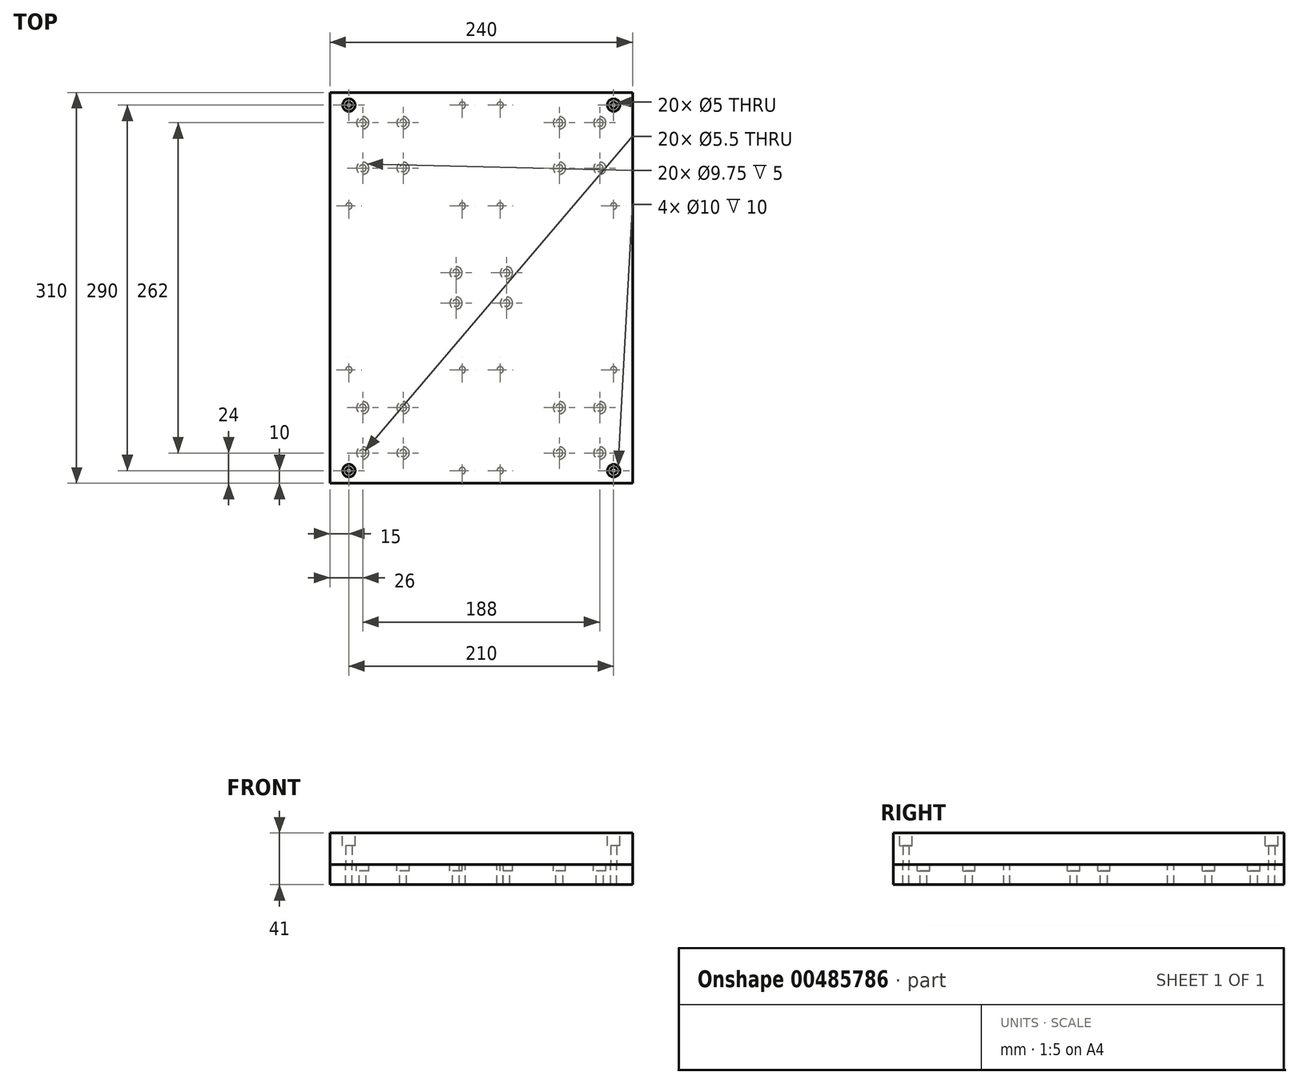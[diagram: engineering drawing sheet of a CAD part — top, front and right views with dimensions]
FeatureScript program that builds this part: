
annotation { "Feature Type Name" : "Feature", "Feature Type Description" : "" }
export const myFeature = defineFeature(function(context is Context, id is Id, definition is map)
    precondition{}
    {
        {
            var Q0;
            Q0=qCreatedBy(makeId("Top.planeOp"),FACE);
            var sketch = newSketch(context, id + "F0", { "sketchPlane" : qUnion([Q0])});
            skLineSegment(sketch, "E0.bottom", {"start": v(120, 155) * mm, "end": v(-120, 155) * mm});
            skLineSegment(sketch, "E0.top", {"start": v(120, -155) * mm, "end": v(-120, -155) * mm});
            skLineSegment(sketch, "E0.left", {"start": v(120, 155) * mm, "end": v(120, -155) * mm});
            skLineSegment(sketch, "E0.right", {"start": v(-120, 155) * mm, "end": v(-120, -155) * mm});
            skPoint(sketch, "E0.middle", {"position": v(0, 0) * mm});
            skLineSegment(sketch, "E1", {"start": v(120, 113) * mm, "end": v(-120, 113) * mm, "construction": true});
            skLineSegment(sketch, "E2", {"start": v(78, 155) * mm, "end": v(78, -155) * mm, "construction": true});
            skLineSegment(sketch, "E3", {"start": v(62, 155) * mm, "end": v(62, -155) * mm, "construction": true});
            skLineSegment(sketch, "E4", {"start": v(94, 155) * mm, "end": v(94, -155) * mm, "construction": true});
            skLineSegment(sketch, "E5", {"start": v(120, 95) * mm, "end": v(-120, 95) * mm, "construction": true});
            skLineSegment(sketch, "E6", {"start": v(120, 131) * mm, "end": v(-120, 131) * mm, "construction": true});
            skPoint(sketch, "E7", {"position": v(94, 131) * mm});
            skPoint(sketch, "E8", {"position": v(94, 95) * mm});
            skPoint(sketch, "E9", {"position": v(62, 95) * mm});
            skPoint(sketch, "E10", {"position": v(62, 131) * mm});
            skLineSegment(sketch, "E11", {"start": v(-62, 155) * mm, "end": v(-62, -155) * mm, "construction": true});
            skLineSegment(sketch, "E12", {"start": v(-78, 155) * mm, "end": v(-78, -155) * mm, "construction": true});
            skLineSegment(sketch, "E13", {"start": v(-94, 155) * mm, "end": v(-94, -155) * mm, "construction": true});
            skLineSegment(sketch, "E14", {"start": v(120, -113) * mm, "end": v(-120, -113) * mm, "construction": true});
            skLineSegment(sketch, "E15", {"start": v(120, -131) * mm, "end": v(-120, -131) * mm, "construction": true});
            skLineSegment(sketch, "E16", {"start": v(120, -95) * mm, "end": v(-120, -95) * mm, "construction": true});
            skPoint(sketch, "E17", {"position": v(-62, 131) * mm});
            skPoint(sketch, "E18", {"position": v(-94, 131) * mm});
            skPoint(sketch, "E19", {"position": v(-62, 95) * mm});
            skPoint(sketch, "E20", {"position": v(-94, 95) * mm});
            skPoint(sketch, "E21", {"position": v(94, -95) * mm});
            skPoint(sketch, "E22", {"position": v(94, -131) * mm});
            skPoint(sketch, "E23", {"position": v(62, -95) * mm});
            skPoint(sketch, "E24", {"position": v(62, -131) * mm});
            skPoint(sketch, "E25", {"position": v(-62, -95) * mm});
            skPoint(sketch, "E26", {"position": v(-62, -131) * mm});
            skPoint(sketch, "E27", {"position": v(-94, -131) * mm});
            skPoint(sketch, "E28", {"position": v(-94, -95) * mm});
            skLineSegment(sketch, "E29.bottom", {"start": v(20, -12) * mm, "end": v(-20, -12) * mm, "construction": true});
            skLineSegment(sketch, "E29.top", {"start": v(20, 12) * mm, "end": v(-20, 12) * mm, "construction": true});
            skLineSegment(sketch, "E29.left", {"start": v(20, -12) * mm, "end": v(20, 12) * mm, "construction": true});
            skLineSegment(sketch, "E29.right", {"start": v(-20, -12) * mm, "end": v(-20, 12) * mm, "construction": true});
            skSolve(sketch);
        }
        {
            var Q0;
            Q0=qSketchRegion(id+"F0",true);
            extrude(context, id + "F1", {"entities" : qUnion([Q0]), "oppositeDirection" : true, "depth" : 16 * mm});
        }
        {
            var Q0;
            Q0=sQuery(id+"F0.wireOp",VERTEX,"E7");
            var Q1;
            Q1=sQuery(id+"F0.wireOp",VERTEX,"E10");
            var Q2;
            Q2=sQuery(id+"F0.wireOp",VERTEX,"E8");
            var Q3;
            Q3=sQuery(id+"F0.wireOp",VERTEX,"E9");
            var Q4;
            Q4=sQuery(id+"F0.wireOp",VERTEX,"E17");
            var Q5;
            Q5=sQuery(id+"F0.wireOp",VERTEX,"E18");
            var Q6;
            Q6=sQuery(id+"F0.wireOp",VERTEX,"E19");
            var Q7;
            Q7=sQuery(id+"F0.wireOp",VERTEX,"E20");
            var Q8;
            Q8=sQuery(id+"F0.wireOp",VERTEX,"E21");
            var Q9;
            Q9=sQuery(id+"F0.wireOp",VERTEX,"E23");
            var Q10;
            Q10=sQuery(id+"F0.wireOp",VERTEX,"E22");
            var Q11;
            Q11=sQuery(id+"F0.wireOp",VERTEX,"E24");
            var Q12;
            Q12=sQuery(id+"F0.wireOp",VERTEX,"E25");
            var Q13;
            Q13=sQuery(id+"F0.wireOp",VERTEX,"E28");
            var Q14;
            Q14=sQuery(id+"F0.wireOp",VERTEX,"E26");
            var Q15;
            Q15=sQuery(id+"F0.wireOp",VERTEX,"E27");
            var Q16;
            Q16=sQuery(id+"F0.wireOp",VERTEX,"E29.left.end");
            var Q17;
            Q17=sQuery(id+"F0.wireOp",VERTEX,"E29.left.start");
            var Q18;
            Q18=sQuery(id+"F0.wireOp",VERTEX,"E29.right.end");
            var Q19;
            Q19=sQuery(id+"F0.wireOp",VERTEX,"E29.right.start");
            var Q20;
            Q20=makeQuery(id+"F1.opExtrude","SWEPT_BODY",BODY,{"disambiguationData":[OSD([sQuery(id+"F0.wireOp",EDGE,"E0.bottom"),sQuery(id+"F0.wireOp",EDGE,"E0.top"),sQuery(id+"F0.wireOp",EDGE,"E0.left"),sQuery(id+"F0.wireOp",EDGE,"E0.right")])]});
            hole(context, id + "F2", {"style" : HoleStyle.C_BORE, "endStyle" : HoleEndStyle.THROUGH, "standardTappedOrClearance" : lookupTablePath({ "standard" : "ISO", "fit" : "Normal", "size" : "M5", "type" : "Clearance" }), "standardBlindInLast" : lookupTablePath({ "fit" : "Standard", "standard" : "ISO", "size" : "M5", "type" : "Clearance" }), "holeDiameter" : 5.5 * mm, "cBoreDiameter" : 9.75 * mm, "cBoreDepth" : 5 * mm, "locations" : qUnion([Q0, Q1, Q2, Q3, Q4, Q5, Q6, Q7, Q8, Q9, Q10, Q11, Q12, Q13, Q14, Q15, Q16, Q17, Q18, Q19]), "scope" : qUnion([Q20]), "isTappedThrough" : true});
        }
        {
            var Q0;
            Q0=makeQuery(id+"F1.opExtrude","CAP_FACE",FACE,{"disambiguationData":[OSD([sQuery(id+"F0.wireOp",EDGE,"E0.bottom"),sQuery(id+"F0.wireOp",EDGE,"E0.top"),sQuery(id+"F0.wireOp",EDGE,"E0.left"),sQuery(id+"F0.wireOp",EDGE,"E0.right")])],"isStart":true});
            var sketch = newSketch(context, id + "F3", { "sketchPlane" : qUnion([Q0])});
            skLineSegment(sketch, "E30", {"start": v(0, 155) * mm, "end": v(0, -155) * mm, "construction": true});
            skLineSegment(sketch, "E31", {"start": v(120, 0) * mm, "end": v(-120, 0) * mm, "construction": true});
            skLineSegment(sketch, "E32", {"start": v(-105, 155) * mm, "end": v(-105, -155) * mm, "construction": true});
            skLineSegment(sketch, "E33", {"start": v(105, 155) * mm, "end": v(105, -155) * mm, "construction": true});
            skLineSegment(sketch, "E34", {"start": v(15, 155) * mm, "end": v(15, -155) * mm, "construction": true});
            skLineSegment(sketch, "E35", {"start": v(-15, 155) * mm, "end": v(-15, -155) * mm, "construction": true});
            skLineSegment(sketch, "E36", {"start": v(-120, 145) * mm, "end": v(120, 145) * mm, "construction": true});
            skLineSegment(sketch, "E37", {"start": v(-120, 65) * mm, "end": v(120, 65) * mm, "construction": true});
            skLineSegment(sketch, "E38", {"start": v(-120, -65) * mm, "end": v(120, -65) * mm, "construction": true});
            skLineSegment(sketch, "E39", {"start": v(-120, -145) * mm, "end": v(120, -145) * mm, "construction": true});
            skPoint(sketch, "E40", {"position": v(-15, 145) * mm});
            skPoint(sketch, "E41", {"position": v(15, 145) * mm});
            skPoint(sketch, "E42", {"position": v(-105, 65) * mm});
            skPoint(sketch, "E43", {"position": v(105, 65) * mm});
            skPoint(sketch, "E44", {"position": v(-105, -65) * mm});
            skPoint(sketch, "E45", {"position": v(105, -65) * mm});
            skPoint(sketch, "E46", {"position": v(-15, -145) * mm});
            skPoint(sketch, "E47", {"position": v(15, -145) * mm});
            skPoint(sketch, "E48", {"position": v(-105, 145) * mm});
            skPoint(sketch, "E49", {"position": v(105, 145) * mm});
            skPoint(sketch, "E50", {"position": v(-15, 65) * mm});
            skPoint(sketch, "E51", {"position": v(15, 65) * mm});
            skPoint(sketch, "E52", {"position": v(15, -65) * mm});
            skPoint(sketch, "E53", {"position": v(-15, -65) * mm});
            skPoint(sketch, "E54", {"position": v(-105, -145) * mm});
            skPoint(sketch, "E55", {"position": v(105, -145) * mm});
            skSolve(sketch);
        }
        {
            var Q0;
            Q0=sQuery(id+"F3.wireOp",VERTEX,"E40");
            var Q1;
            Q1=sQuery(id+"F3.wireOp",VERTEX,"E41");
            var Q2;
            Q2=sQuery(id+"F3.wireOp",VERTEX,"E42");
            var Q3;
            Q3=sQuery(id+"F3.wireOp",VERTEX,"E43");
            var Q4;
            Q4=sQuery(id+"F3.wireOp",VERTEX,"E44");
            var Q5;
            Q5=sQuery(id+"F3.wireOp",VERTEX,"E45");
            var Q6;
            Q6=sQuery(id+"F3.wireOp",VERTEX,"E46");
            var Q7;
            Q7=sQuery(id+"F3.wireOp",VERTEX,"E47");
            var Q8;
            Q8=sQuery(id+"F3.wireOp",VERTEX,"E54");
            var Q9;
            Q9=sQuery(id+"F3.wireOp",VERTEX,"E55");
            var Q10;
            Q10=sQuery(id+"F3.wireOp",VERTEX,"E49");
            var Q11;
            Q11=sQuery(id+"F3.wireOp",VERTEX,"E48");
            var Q12;
            Q12=sQuery(id+"F3.wireOp",VERTEX,"E50");
            var Q13;
            Q13=sQuery(id+"F3.wireOp",VERTEX,"E51");
            var Q14;
            Q14=sQuery(id+"F3.wireOp",VERTEX,"E53");
            var Q15;
            Q15=sQuery(id+"F3.wireOp",VERTEX,"E52");
            var Q16;
            Q16=makeQuery(id+"F1.opExtrude","SWEPT_BODY",BODY,{"disambiguationData":[OSD([sQuery(id+"F0.wireOp",EDGE,"E0.bottom"),sQuery(id+"F0.wireOp",EDGE,"E0.top"),sQuery(id+"F0.wireOp",EDGE,"E0.left"),sQuery(id+"F0.wireOp",EDGE,"E0.right")])]});
            hole(context, id + "F4", {"style" : HoleStyle.SIMPLE, "endStyle" : HoleEndStyle.BLIND, "holeDiameter" : 5 * mm, "holeDepth" : 20 * mm, "isTappedThrough" : true, "tappedDepth" : 18.5 * mm, "tapClearance" : 3, "locations" : qUnion([Q0, Q1, Q2, Q3, Q4, Q5, Q6, Q7, Q8, Q9, Q10, Q11, Q12, Q13, Q14, Q15]), "scope" : qUnion([Q16])});
        }
        {
            var Q0;
            Q0=makeQuery(id+"F1.opExtrude","CAP_FACE",FACE,{"disambiguationData":[OSD([sQuery(id+"F0.wireOp",EDGE,"E0.bottom"),sQuery(id+"F0.wireOp",EDGE,"E0.top"),sQuery(id+"F0.wireOp",EDGE,"E0.left"),sQuery(id+"F0.wireOp",EDGE,"E0.right")])],"isStart":true});
            var sketch = newSketch(context, id + "F5", { "sketchPlane" : qUnion([Q0])});
            skLineSegment(sketch, "E56.bottom", {"start": v(-120, -155) * mm, "end": v(120, -155) * mm});
            skLineSegment(sketch, "E56.top", {"start": v(-120, 155) * mm, "end": v(120, 155) * mm});
            skLineSegment(sketch, "E56.left", {"start": v(-120, -155) * mm, "end": v(-120, 155) * mm});
            skLineSegment(sketch, "E56.right", {"start": v(120, -155) * mm, "end": v(120, 155) * mm});
            skCircle(sketch, "E57.0", {"center": v(-105, -145) * mm, "radius": 2.5 * mm});
            skCircle(sketch, "E58.0", {"center": v(105, -145) * mm, "radius": 2.5 * mm});
            skCircle(sketch, "E59.0", {"center": v(105, 145) * mm, "radius": 2.5 * mm});
            skCircle(sketch, "E60.0", {"center": v(-105, 145) * mm, "radius": 2.5 * mm});
            skSolve(sketch);
        }
        {
            var Q0;
            Q0 = qSketchRegion(id + "F5", true);
            extrude(context, id + "F6", {"entities" : qUnion([Q0]), "depth" : 25 * mm});
        }
        {
            var Q0;
            Q0=makeQuery(id+"F6.opExtrude","CAP_FACE",FACE,{"disambiguationData":[OSD([sQuery(id+"F5.wireOp",EDGE,"E56.bottom"),sQuery(id+"F5.wireOp",EDGE,"E56.top"),sQuery(id+"F5.wireOp",EDGE,"E56.left"),sQuery(id+"F5.wireOp",EDGE,"E56.right"),sQuery(id+"F5.wireOp",EDGE,"E57.0"),sQuery(id+"F5.wireOp",EDGE,"E58.0"),sQuery(id+"F5.wireOp",EDGE,"E59.0"),sQuery(id+"F5.wireOp",EDGE,"E60.0")])],"isStart":false});
            var sketch = newSketch(context, id + "F7", { "sketchPlane" : qUnion([Q0])});
            skCircle(sketch, "E61", {"center": v(-105, -145) * mm, "radius": 5 * mm});
            skCircle(sketch, "E62", {"center": v(105, -145) * mm, "radius": 5 * mm});
            skCircle(sketch, "E63", {"center": v(105, 145) * mm, "radius": 5 * mm});
            skCircle(sketch, "E64", {"center": v(-105, 145) * mm, "radius": 5 * mm});
            skSolve(sketch);
        }
        {
            var Q0;
            Q0 = qSketchRegion(id + "F7", true);
            extrude(context, id + "F8", {"entities" : qUnion([Q0]), "operationType" : NewBodyOperationType.REMOVE, "oppositeDirection" : true, "depth" : 10 * mm});
        }
    });
